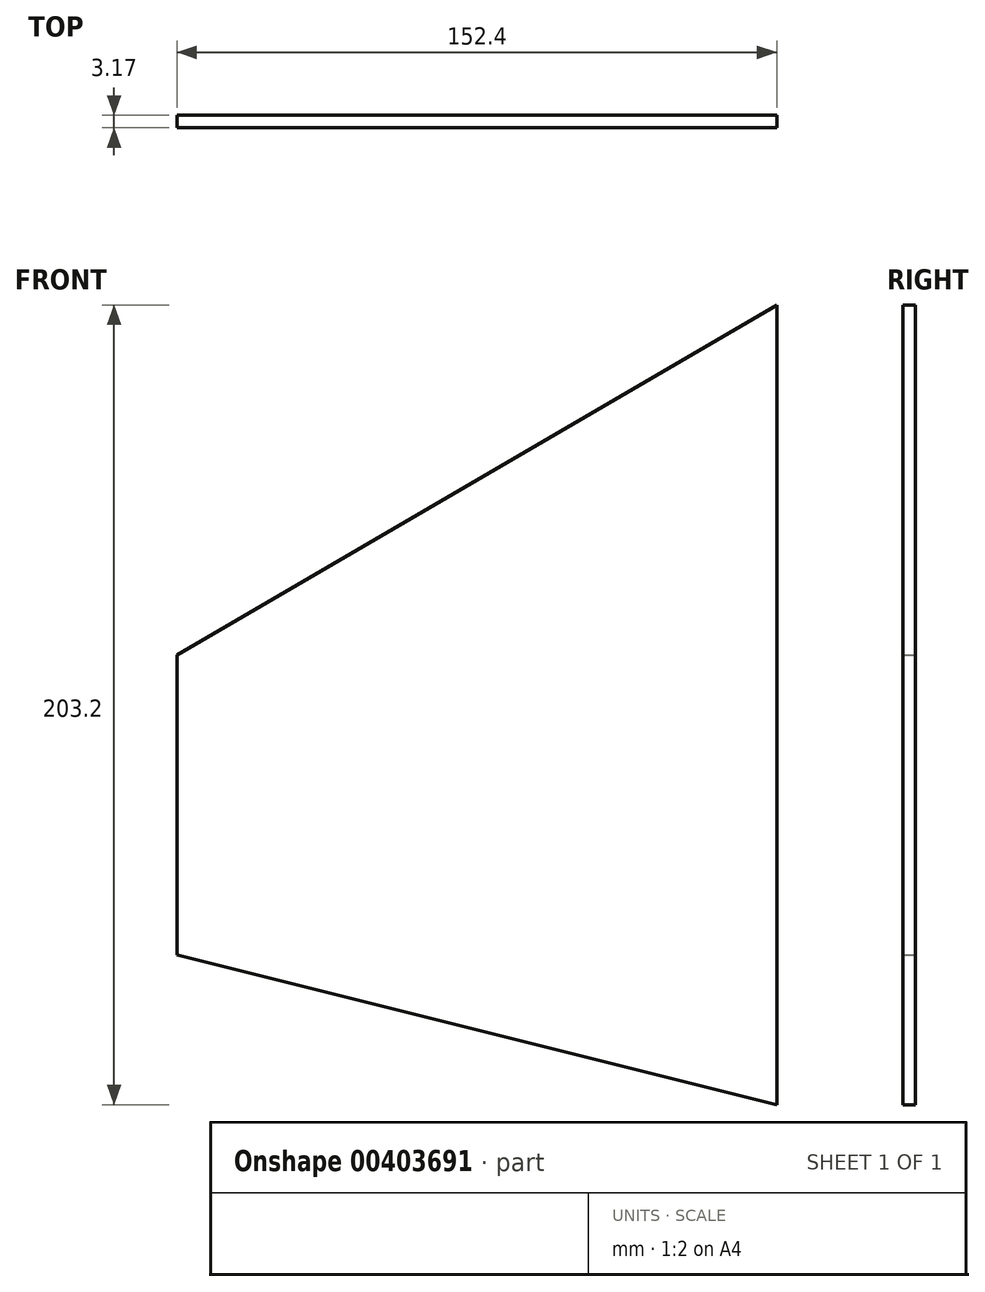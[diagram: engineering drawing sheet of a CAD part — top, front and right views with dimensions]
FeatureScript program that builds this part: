
annotation { "Feature Type Name" : "Feature", "Feature Type Description" : "" }
export const myFeature = defineFeature(function(context is Context, id is Id, definition is map)
    precondition{}
    {
        {
            var Q0;
            Q0=qCreatedBy(makeId("Front.planeOp"),FACE);
            var sketch = newSketch(context, id + "F0", { "sketchPlane" : qUnion([Q0])});
            skLineSegment(sketch, "E0", {"start": v(0, 0) * mm, "end": v(0, 203.2) * mm});
            skLineSegment(sketch, "E1", {"start": v(0, 203.2) * mm, "end": v(-152.4, 114.3) * mm});
            skLineSegment(sketch, "E2", {"start": v(-152.4, 114.3) * mm, "end": v(-152.4, 38.1) * mm});
            skLineSegment(sketch, "E3", {"start": v(-152.4, 38.1) * mm, "end": v(0, 0) * mm});
            skSolve(sketch);
        }
        {
            var Q0;
            Q0=makeQuery(id+"F0.imprint","IMPRINT",FACE,{"disambiguationData":[TD([[makeQuery(id+"F0.imprint","IMPRINT",EDGE,{"derivedFrom":sQuery(id+"F0.wireOp",EDGE,"E0")}),1.0]])]});
            extrude(context, id + "F1", {"entities" : qUnion([Q0]), "depth" : 3.17 * mm});
        }
    });
